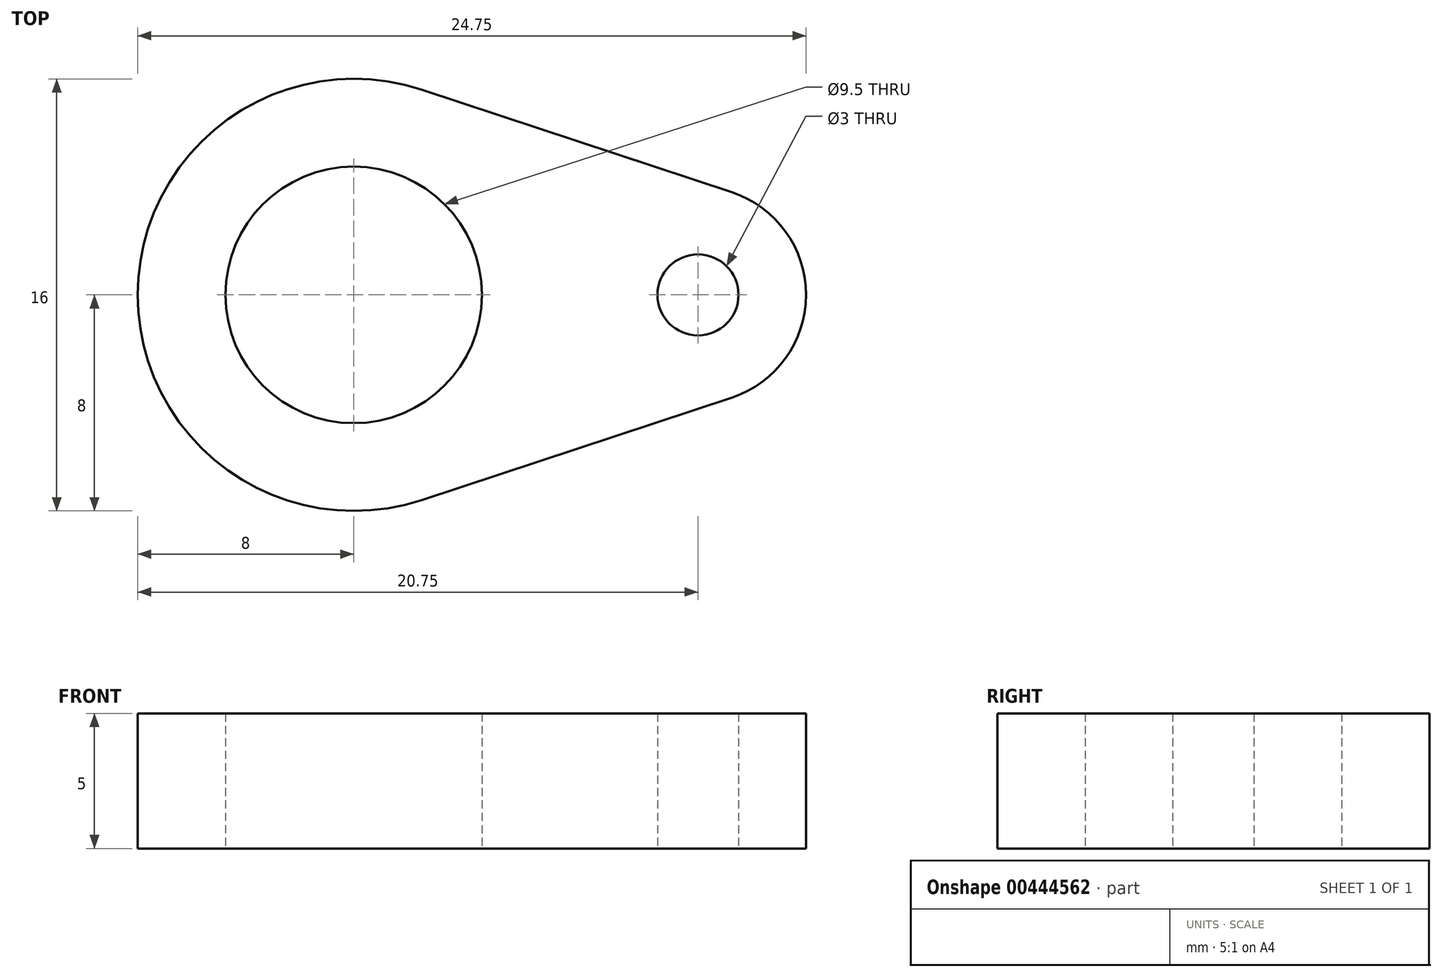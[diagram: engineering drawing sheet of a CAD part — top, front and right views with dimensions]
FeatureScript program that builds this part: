
annotation { "Feature Type Name" : "Feature", "Feature Type Description" : "" }
export const myFeature = defineFeature(function(context is Context, id is Id, definition is map)
    precondition{}
    {
        {
            var Q0;
            Q0=qCreatedBy(makeId("Top.planeOp"),FACE);
            var sketch = newSketch(context, id + "F0", { "sketchPlane" : qUnion([Q0])});
            skCircle(sketch, "E0", {"center": v(0, 0) * mm, "radius": 4.75 * mm});
            skPoint(sketch, "E1", {"position": v(12.75, 0) * mm});
            skCircle(sketch, "E2", {"center": v(12.75, 0) * mm, "radius": 1.5 * mm});
            skArc(sketch, "E3", {"start": v(12.75, 4) * mm, "mid": v(16.75, 0) * mm, "end": v(12.75, -4) * mm});
            skCircle(sketch, "E4", {"center": v(0, 0) * mm, "radius": 8 * mm});
            skLineSegment(sketch, "E5", {"start": v(-7.3, 10.84) * mm, "end": v(23.96, 0.51) * mm});
            skLineSegment(sketch, "E6", {"start": v(0, -8.43) * mm, "end": v(25.19, -0.1) * mm});
            skSolve(sketch);
        }
        {
            var Q0;
            Q0=makeQuery(id+"F0.imprint","IMPRINT",FACE,{"disambiguationData":[TD([[makeQuery(id+"F0.imprint","IMPRINT",EDGE,{"derivedFrom":sQuery(id+"F0.wireOp",EDGE,"E0")}),-1.0]])]});
            var Q1;
            {var subQ0=sQuery(id+"F0.wireOp",EDGE,"E5");var subQ1=sQuery(id+"F0.wireOp",EDGE,"E3");var subQ2=makeQuery(id+"F0.imprint","INTERSECT",VERTEX,{"derivedFrom":[subQ1,subQ0]});Q1=makeQuery(id+"F0.imprint","IMPRINT",FACE,{"disambiguationData":[TD([[makeQuery(id+"F0.imprint","IMPRINT",EDGE,{"disambiguationData":[TD([[subQ2,1.0]])],"derivedFrom":subQ1}),1.0]])]});}
            var Q2;
            {var subQ0=sQuery(id+"F0.wireOp",EDGE,"E3");var subQ1=makeQuery(id+"F0.imprint","INTERSECT",VERTEX,{"derivedFrom":[subQ0,sQuery(id+"F0.wireOp",EDGE,"E5")]});Q2=makeQuery(id+"F0.imprint","IMPRINT",FACE,{"disambiguationData":[TD([[makeQuery(id+"F0.imprint","IMPRINT",EDGE,{"disambiguationData":[TD([[subQ1,1.0]])],"derivedFrom":subQ0}),-1.0]])]});}
            var Q3;
            {var subQ0=sQuery(id+"F0.wireOp",EDGE,"E6");var subQ1=sQuery(id+"F0.wireOp",EDGE,"E3");var subQ2=makeQuery(id+"F0.imprint","INTERSECT",VERTEX,{"derivedFrom":[subQ1,subQ0]});Q3=makeQuery(id+"F0.imprint","IMPRINT",FACE,{"disambiguationData":[TD([[makeQuery(id+"F0.imprint","IMPRINT",EDGE,{"disambiguationData":[TD([[subQ2,-1.0]])],"derivedFrom":subQ1}),1.0]])]});}
            var Q4;
            Q4=makeQuery(id+"F0.imprint","IMPRINT",FACE,{"disambiguationData":[TD([[makeQuery(id+"F0.imprint","IMPRINT",EDGE,{"derivedFrom":sQuery(id+"F0.wireOp",EDGE,"E2")}),-1.0]])]});
            extrude(context, id + "F1", {"entities" : qUnion([Q0, Q1, Q2, Q3, Q4]), "depth" : 5 * mm});
        }
    });
